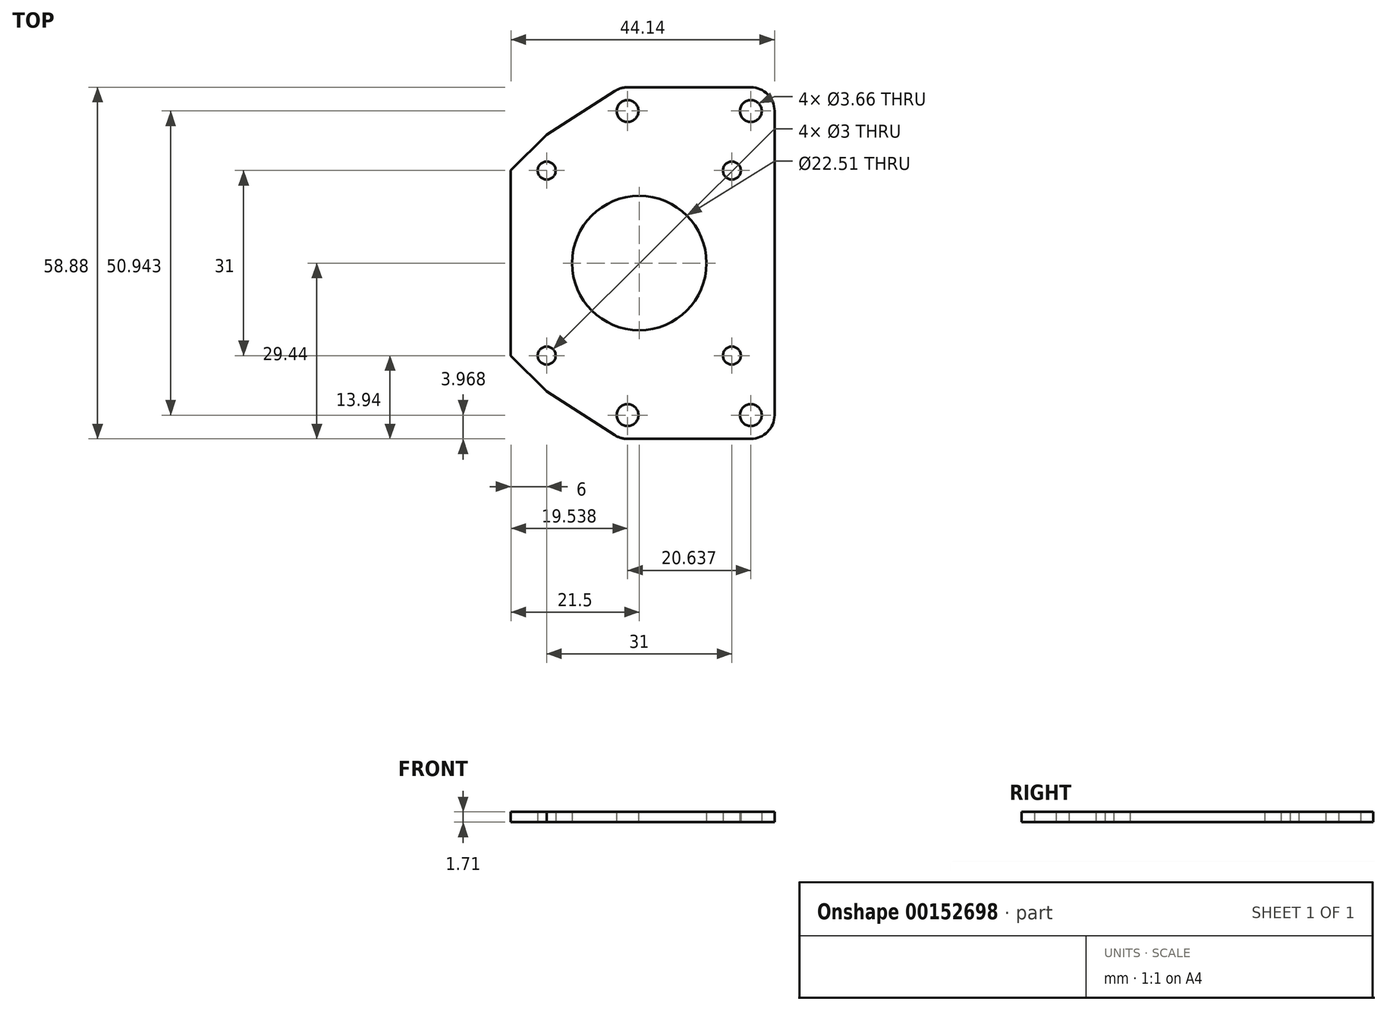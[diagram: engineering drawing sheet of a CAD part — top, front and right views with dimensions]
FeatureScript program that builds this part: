
annotation { "Feature Type Name" : "Feature", "Feature Type Description" : "" }
export const myFeature = defineFeature(function(context is Context, id is Id, definition is map)
    precondition{}
    {
        {
            var Q0;
            Q0=qCreatedBy(makeId("Top.planeOp"),FACE);
            var sketch = newSketch(context, id + "F0", { "sketchPlane" : qUnion([Q0])});
            skLineSegment(sketch, "E0.bottom", {"start": v(15.5, 15.5) * mm, "end": v(-15.5, 15.5) * mm, "construction": true});
            skLineSegment(sketch, "E0.top", {"start": v(15.5, -15.5) * mm, "end": v(-15.5, -15.5) * mm, "construction": true});
            skLineSegment(sketch, "E0.left", {"start": v(15.5, 15.5) * mm, "end": v(15.5, -15.5) * mm, "construction": true});
            skLineSegment(sketch, "E0.right", {"start": v(-15.5, 15.5) * mm, "end": v(-15.5, -15.5) * mm, "construction": true});
            skPoint(sketch, "E0.middle", {"position": v(0, 0) * mm});
            skCircle(sketch, "E1", {"center": v(0, 0) * mm, "radius": 11.25 * mm});
            skCircle(sketch, "E2", {"center": v(-15.5, 15.5) * mm, "radius": 1.5 * mm});
            skCircle(sketch, "E3", {"center": v(15.5, 15.5) * mm, "radius": 1.5 * mm});
            skCircle(sketch, "E4", {"center": v(15.5, -15.5) * mm, "radius": 1.5 * mm});
            skCircle(sketch, "E5", {"center": v(-15.5, -15.5) * mm, "radius": 1.5 * mm});
            skLineSegment(sketch, "E6", {"start": v(0, 0) * mm, "end": v(-21.5, 0) * mm, "construction": true});
            skLineSegment(sketch, "E7", {"start": v(0, 0) * mm, "end": v(22.64, 0) * mm, "construction": true});
            skLineSegment(sketch, "E8", {"start": v(-21.5, -15.5) * mm, "end": v(-21.5, 15.5) * mm});
            skLineSegment(sketch, "E9", {"start": v(-21.5, 15.5) * mm, "end": v(-15.5, 21.5) * mm});
            skLineSegment(sketch, "E10", {"start": v(-21.5, -15.5) * mm, "end": v(-15.5, -21.5) * mm});
            skLineSegment(sketch, "E11", {"start": v(-15.5, -21.5) * mm, "end": v(-4.1, -28.81) * mm});
            skLineSegment(sketch, "E12", {"start": v(-15.5, 21.5) * mm, "end": v(-4.1, 28.81) * mm});
            skLineSegment(sketch, "E13", {"start": v(22.64, -29.44) * mm, "end": v(22.64, 29.44) * mm});
            skLineSegment(sketch, "E14", {"start": v(22.64, 29.44) * mm, "end": v(-1.96, 29.44) * mm});
            skLineSegment(sketch, "E15", {"start": v(22.64, -29.44) * mm, "end": v(-1.96, -29.44) * mm});
            skArc(sketch, "E16", {"start": v(-1.96, 29.44) * mm, "mid": v(-3.08, 29.28) * mm, "end": v(-4.1, 28.81) * mm});
            skArc(sketch, "E17", {"start": v(-4.1, -28.81) * mm, "mid": v(-3.08, -29.28) * mm, "end": v(-1.96, -29.44) * mm});
            skCircle(sketch, "E18", {"center": v(-1.96, -25.47) * mm, "radius": 1.83 * mm});
            skCircle(sketch, "E19", {"center": v(-1.96, 25.47) * mm, "radius": 1.83 * mm});
            skLineSegment(sketch, "E20", {"start": v(18.67, -29.44) * mm, "end": v(18.67, -25.47) * mm, "construction": true});
            skLineSegment(sketch, "E21", {"start": v(18.67, -25.47) * mm, "end": v(22.64, -25.47) * mm, "construction": true});
            skLineSegment(sketch, "E22", {"start": v(18.67, 29.44) * mm, "end": v(18.67, 25.47) * mm, "construction": true});
            skCircle(sketch, "E23", {"center": v(18.67, -25.47) * mm, "radius": 1.83 * mm});
            skCircle(sketch, "E24", {"center": v(18.67, 25.47) * mm, "radius": 1.83 * mm});
            skSolve(sketch);
        }
        {
            var Q0;
            Q0 = qSketchRegion(id + "F0", true);
            extrude(context, id + "F1", {"entities" : qUnion([Q0]), "depth" : 1.7 * mm});
        }
        {
            var Q0;
            Q0=makeQuery(id+"F1.opExtrude","SWEPT_EDGE",EDGE,{"disambiguationData":[OSD([sQuery(id+"F0.wireOp",EDGE,"E13"),sQuery(id+"F0.wireOp",EDGE,"E15")])]});
            var Q1;
            Q1=makeQuery(id+"F1.opExtrude","SWEPT_EDGE",EDGE,{"disambiguationData":[OSD([sQuery(id+"F0.wireOp",EDGE,"E13"),sQuery(id+"F0.wireOp",EDGE,"E14")])]});
            fillet(context, id + "F2", {"entities" : qUnion([Q0, Q1]), "radius" : 3.97 * mm, "tangentPropagation" : true, "allowEdgeOverflow" : false});
        }
    });
